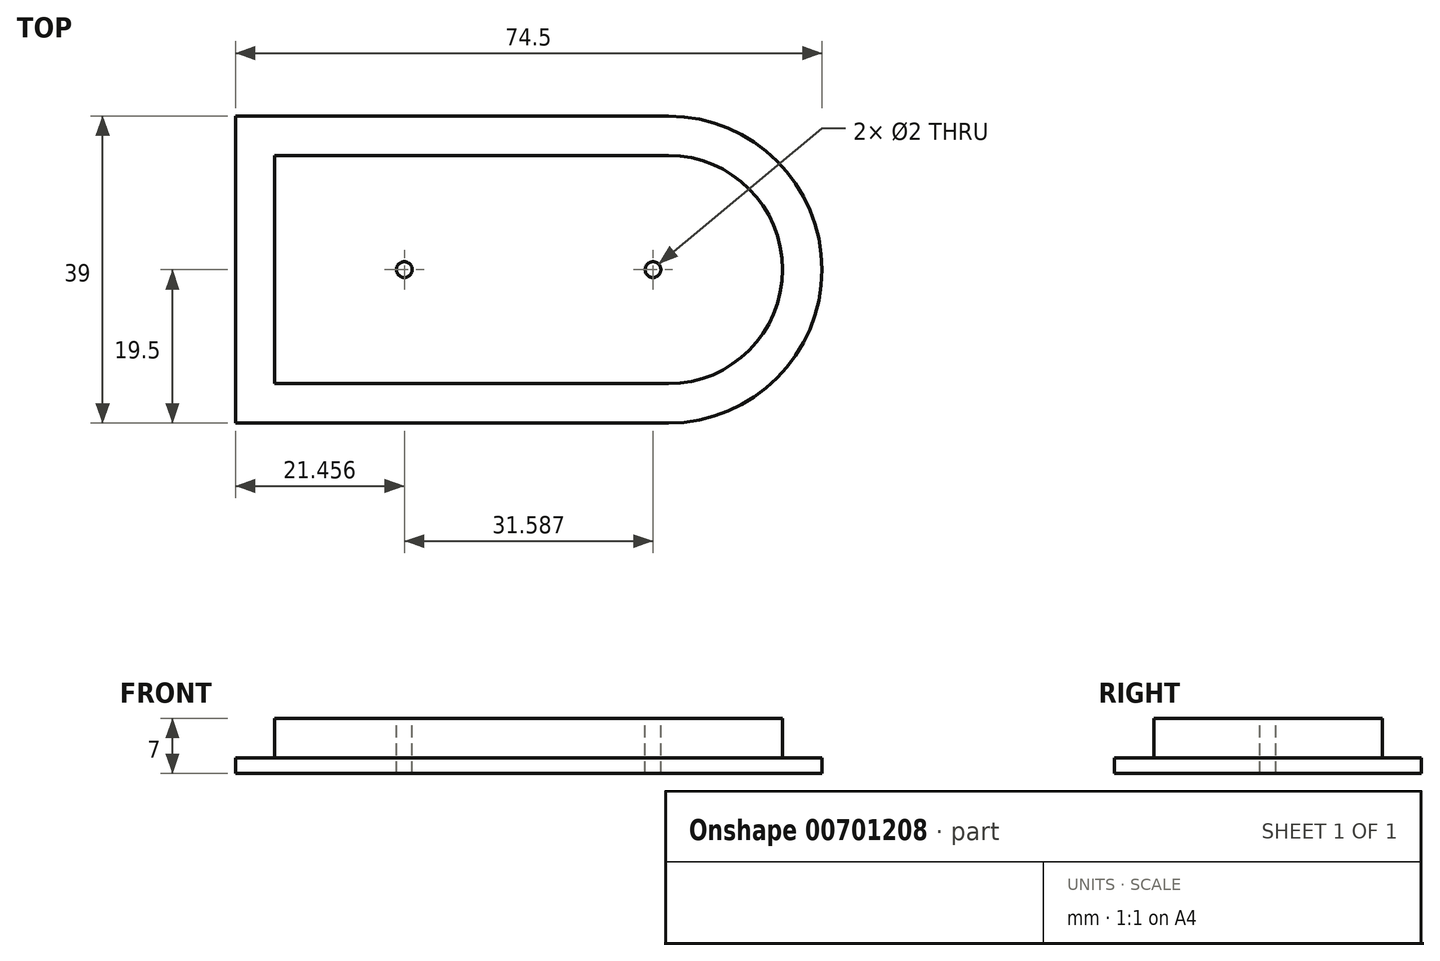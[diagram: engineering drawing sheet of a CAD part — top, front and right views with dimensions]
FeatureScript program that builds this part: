
annotation { "Feature Type Name" : "Feature", "Feature Type Description" : "" }
export const myFeature = defineFeature(function(context is Context, id is Id, definition is map)
    precondition{}
    {
        {
            var Q0;
            Q0=qCreatedBy(makeId("Top.planeOp"),FACE);
            var sketch = newSketch(context, id + "F0", { "sketchPlane" : qUnion([Q0])});
            skLineSegment(sketch, "E0.bottom", {"start": v(-25, -14.5) * mm, "end": v(25, -14.5) * mm});
            skLineSegment(sketch, "E0.top", {"start": v(-25, 14.5) * mm, "end": v(25, 14.5) * mm});
            skLineSegment(sketch, "E0.right", {"start": v(25, -14.5) * mm, "end": v(25, 14.5) * mm});
            skPoint(sketch, "E0.middle", {"position": v(0, 0) * mm});
            skArc(sketch, "E1", {"start": v(-25, 14.5) * mm, "mid": v(-39.5, 0) * mm, "end": v(-25, -14.5) * mm});
            skSolve(sketch);
        }
        {
            var Q0;
            Q0 = qSketchRegion(id + "F0", true);
            extrude(context, id + "F1", {"entities" : qUnion([Q0]), "depth" : 5 * mm, "offsetDistance" : 25 * mm});
        }
        {
            var Q0;
            Q0=makeQuery(id+"F1.opExtrude","CAP_FACE",FACE,{"disambiguationData":[OSD([sQuery(id+"F0.wireOp",EDGE,"E0.bottom"),sQuery(id+"F0.wireOp",EDGE,"E0.top"),sQuery(id+"F0.wireOp",EDGE,"E0.right"),sQuery(id+"F0.wireOp",EDGE,"E1")])],"isStart":false});
            var sketch = newSketch(context, id + "F2", { "sketchPlane" : qUnion([Q0])});
            skLineSegment(sketch, "E2.1", {"start": v(25, -14.5) * mm, "end": v(25, 14.5) * mm, "construction": true});
            skLineSegment(sketch, "E2.2", {"start": v(-25, 14.5) * mm, "end": v(25, 14.5) * mm, "construction": true});
            skArc(sketch, "E2.3", {"start": v(-25, 14.5) * mm, "mid": v(-39.5, 0) * mm, "end": v(-25, -14.5) * mm, "construction": true});
            skLineSegment(sketch, "E2.4", {"start": v(-25, -14.5) * mm, "end": v(25, -14.5) * mm, "construction": true});
            skLineSegment(sketch, "E3.0", {"start": v(30, -19.5) * mm, "end": v(30, 19.5) * mm});
            skLineSegment(sketch, "E3.1", {"start": v(-25, -19.5) * mm, "end": v(30, -19.5) * mm});
            skArc(sketch, "E3.2", {"start": v(-25, 19.5) * mm, "mid": v(-44.5, 0) * mm, "end": v(-25, -19.5) * mm});
            skLineSegment(sketch, "E3.3", {"start": v(-25, 19.5) * mm, "end": v(30, 19.5) * mm});
            skSolve(sketch);
        }
        {
            var Q0;
            Q0 = qSketchRegion(id + "F2", true);
            extrude(context, id + "F3", {"entities" : qUnion([Q0]), "operationType" : NewBodyOperationType.ADD, "depth" : 2 * mm, "offsetDistance" : 25 * mm});
        }
        {
            var Q0;
            Q0=makeQuery(id+"F1.opExtrude","CAP_FACE",FACE,{"disambiguationData":[OSD([sQuery(id+"F0.wireOp",EDGE,"E0.bottom"),sQuery(id+"F0.wireOp",EDGE,"E0.top"),sQuery(id+"F0.wireOp",EDGE,"E0.right"),sQuery(id+"F0.wireOp",EDGE,"E1")])],"isStart":true});
            var sketch = newSketch(context, id + "F4", { "sketchPlane" : qUnion([Q0])});
            skCircle(sketch, "E4", {"center": v(8.54, 0) * mm, "radius": 1 * mm});
            skPoint(sketch, "E4.centerSnap0", {"position": v(25, 0) * mm});
            skLineSegment(sketch, "E5", {"start": v(25, 0) * mm, "end": v(-39.5, 0) * mm, "construction": true});
            skLineSegment(sketch, "E6", {"start": v(-7.25, 0) * mm, "end": v(-7.25, -14.5) * mm, "construction": true});
            skCircle(sketch, "E7.MirrorC", {"center": v(-23.04, 0) * mm, "radius": 1 * mm});
            skSolve(sketch);
        }
        {
            var Q0;
            Q0 = qSketchRegion(id + "F4", true);
            extrude(context, id + "F5", {"entities" : qUnion([Q0]), "operationType" : NewBodyOperationType.REMOVE, "oppositeDirection" : true, "depth" : 25 * mm, "offsetDistance" : 25 * mm});
        }
        {
            var Q0;
            Q0=makeQuery(id+"F1.opExtrude","SWEPT_BODY",BODY,{"disambiguationData":[OSD([sQuery(id+"F0.wireOp",EDGE,"E0.bottom"),sQuery(id+"F0.wireOp",EDGE,"E0.top"),sQuery(id+"F0.wireOp",EDGE,"E0.right"),sQuery(id+"F0.wireOp",EDGE,"E1")])]});
            var Q1;
            Q1=makeQuery(id+"F3.opExtrude","CAP_EDGE",EDGE,{"disambiguationData":[OSD([sQuery(id+"F2.wireOp",EDGE,"E3.0")])],"isStart":false});
            transform(context, id + "F6", {"entities" : qUnion([Q0]), "transformType" : TransformType.ROTATION, "transformAxis" : qUnion([Q1]), "angle" : 180 * degree, "makeCopy" : false});
        }
        {
            var Q0;
            Q0=makeQuery(id+"F1.opExtrude","SWEPT_BODY",BODY,{"disambiguationData":[OSD([sQuery(id+"F0.wireOp",EDGE,"E0.bottom"),sQuery(id+"F0.wireOp",EDGE,"E0.top"),sQuery(id+"F0.wireOp",EDGE,"E0.right"),sQuery(id+"F0.wireOp",EDGE,"E1")])]});
            transform(context, id + "F7", {"entities" : qUnion([Q0]), "transformType" : TransformType.TRANSLATION_3D, "dx" : -64.7 * mm, "dy" : 0 * mm, "dz" : -7 * mm, "makeCopy" : false});
        }
    });
